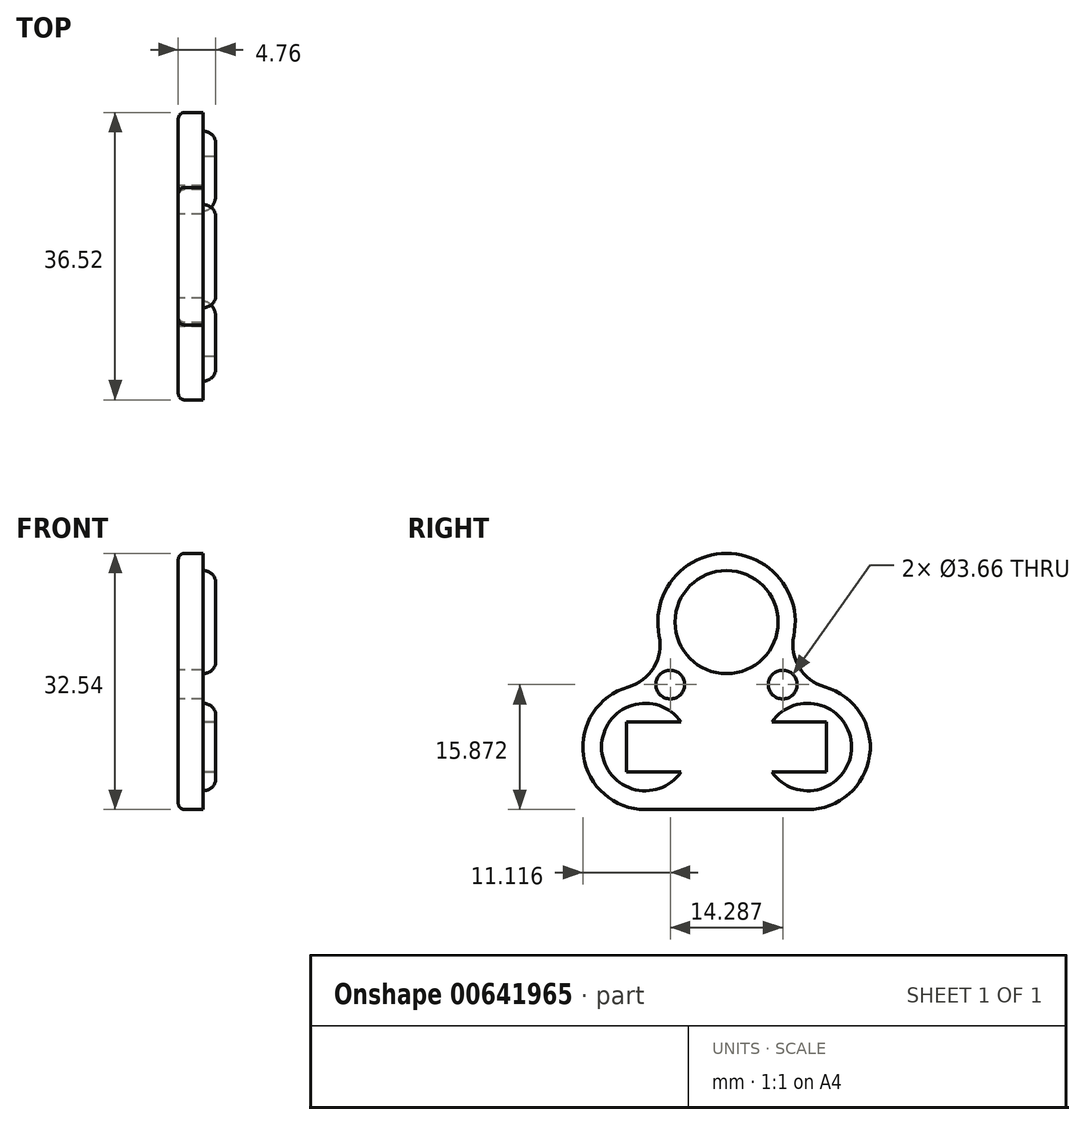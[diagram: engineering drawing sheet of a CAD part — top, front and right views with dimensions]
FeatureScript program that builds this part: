
annotation { "Feature Type Name" : "Feature", "Feature Type Description" : "" }
export const myFeature = defineFeature(function(context is Context, id is Id, definition is map)
    precondition{}
    {
        {
            var Q0;
            Q0=qCreatedBy(makeId("Right.planeOp"),FACE);
            var sketch = newSketch(context, id + "F0", { "sketchPlane" : qUnion([Q0])});
            skCircle(sketch, "E0", {"center": v(0, 0) * mm, "radius": 6.55 * mm});
            skCircle(sketch, "E1", {"center": v(0, 0) * mm, "radius": 8.73 * mm});
            skCircle(sketch, "E2", {"center": v(-10.32, -15.87) * mm, "radius": 5.56 * mm});
            skCircle(sketch, "E3", {"center": v(-10.32, -15.87) * mm, "radius": 7.94 * mm});
            skCircle(sketch, "E4", {"center": v(10.32, -15.87) * mm, "radius": 5.56 * mm});
            skCircle(sketch, "E5", {"center": v(10.32, -15.87) * mm, "radius": 7.94 * mm});
            skArc(sketch, "E6", {"start": v(-12.48, -8.24) * mm, "mid": v(-9.24, -5.77) * mm, "end": v(-8.55, -1.77) * mm});
            skArc(sketch, "E7", {"start": v(8.55, -1.77) * mm, "mid": v(9.24, -5.77) * mm, "end": v(12.48, -8.24) * mm});
            skLineSegment(sketch, "E8", {"start": v(-10.32, -23.81) * mm, "end": v(10.32, -23.81) * mm});
            skSolve(sketch);
        }
        {
            var Q0;
            Q0=makeQuery(id+"F0.imprint","IMPRINT",FACE,{"disambiguationData":[TD([[makeQuery(id+"F0.imprint","IMPRINT",EDGE,{"derivedFrom":sQuery(id+"F0.wireOp",EDGE,"E0")}),-1.0]])]});
            var Q1;
            {var subQ0=sQuery(id+"F0.wireOp",EDGE,"E6");Q1=makeQuery(id+"F0.imprint","IMPRINT",FACE,{"disambiguationData":[TD([[makeQuery(id+"F0.imprint","IMPRINT",EDGE,{"derivedFrom":subQ0}),-1.0]])]});}
            var Q2;
            Q2=makeQuery(id+"F0.imprint","IMPRINT",FACE,{"disambiguationData":[TD([[makeQuery(id+"F0.imprint","IMPRINT",EDGE,{"derivedFrom":sQuery(id+"F0.wireOp",EDGE,"E4")}),-1.0]])]});
            var Q3;
            Q3=makeQuery(id+"F0.imprint","IMPRINT",FACE,{"disambiguationData":[TD([[makeQuery(id+"F0.imprint","IMPRINT",EDGE,{"derivedFrom":sQuery(id+"F0.wireOp",EDGE,"E2")}),-1.0]])]});
            var Q4;
            Q4=makeQuery(id+"F0.imprint","IMPRINT",FACE,{"disambiguationData":[TD([[makeQuery(id+"F0.imprint","IMPRINT",EDGE,{"derivedFrom":sQuery(id+"F0.wireOp",EDGE,"E4")}),1.0]])]});
            var Q5;
            Q5=makeQuery(id+"F0.imprint","IMPRINT",FACE,{"disambiguationData":[TD([[makeQuery(id+"F0.imprint","IMPRINT",EDGE,{"derivedFrom":sQuery(id+"F0.wireOp",EDGE,"E0")}),1.0]])]});
            var Q6;
            Q6=makeQuery(id+"F0.imprint","IMPRINT",FACE,{"disambiguationData":[TD([[makeQuery(id+"F0.imprint","IMPRINT",EDGE,{"derivedFrom":sQuery(id+"F0.wireOp",EDGE,"E2")}),1.0]])]});
            extrude(context, id + "F1", {"entities" : qUnion([Q0, Q1, Q2, Q3, Q4, Q5, Q6]), "depth" : 3.17 * mm, "offsetDistance" : 25.4 * mm});
        }
        {
            var Q0;
            Q0=makeQuery(id+"F0.imprint","IMPRINT",FACE,{"disambiguationData":[TD([[makeQuery(id+"F0.imprint","IMPRINT",EDGE,{"derivedFrom":sQuery(id+"F0.wireOp",EDGE,"E4")}),1.0]])]});
            var Q1;
            Q1=makeQuery(id+"F0.imprint","IMPRINT",FACE,{"disambiguationData":[TD([[makeQuery(id+"F0.imprint","IMPRINT",EDGE,{"derivedFrom":sQuery(id+"F0.wireOp",EDGE,"E2")}),1.0]])]});
            var Q2;
            Q2=makeQuery(id+"F0.imprint","IMPRINT",FACE,{"disambiguationData":[TD([[makeQuery(id+"F0.imprint","IMPRINT",EDGE,{"derivedFrom":sQuery(id+"F0.wireOp",EDGE,"E0")}),1.0]])]});
            extrude(context, id + "F2", {"entities" : qUnion([Q0, Q1, Q2]), "operationType" : NewBodyOperationType.ADD, "depth" : 4.76 * mm, "offsetDistance" : 25.4 * mm});
        }
        {
            var Q0;
            Q0=makeQuery(id+"F2.opExtrude","CAP_EDGE",EDGE,{"disambiguationData":[OSD([sQuery(id+"F0.wireOp",EDGE,"E0")])],"isStart":false});
            var Q1;
            Q1=makeQuery(id+"F2.opExtrude","CAP_EDGE",EDGE,{"disambiguationData":[OSD([sQuery(id+"F0.wireOp",EDGE,"E4")])],"isStart":false});
            var Q2;
            Q2=makeQuery(id+"F2.opExtrude","CAP_EDGE",EDGE,{"disambiguationData":[OSD([sQuery(id+"F0.wireOp",EDGE,"E2")])],"isStart":false});
            fillet(context, id + "F3", {"entities" : qUnion([Q0, Q1, Q2]), "radius" : 1.59 * mm, "tangentPropagation" : true, "allowEdgeOverflow" : false});
        }
        {
            var Q0;
            {var subQ0=sQuery(id+"F0.wireOp",EDGE,"E6");Q0=makeQuery(id+"F0.imprint","IMPRINT",FACE,{"disambiguationData":[TD([[makeQuery(id+"F0.imprint","IMPRINT",EDGE,{"derivedFrom":subQ0}),-1.0]])]});}
            var sketch = newSketch(context, id + "F4", { "sketchPlane" : qUnion([Q0])});
            skPoint(sketch, "E9", {"position": v(-7.14, -7.94) * mm});
            skPoint(sketch, "E10", {"position": v(7.14, -7.94) * mm});
            skSolve(sketch);
        }
        {
            var Q0;
            Q0=sQuery(id+"F4.wireOp",VERTEX,"E10");
            var Q1;
            Q1=sQuery(id+"F4.wireOp",VERTEX,"E9");
            var Q2;
            Q2=makeQuery(id+"F1.opExtrude","SWEPT_BODY",BODY,{"disambiguationData":[OSD([sQuery(id+"F0.wireOp",EDGE,"E1"),sQuery(id+"F0.wireOp",EDGE,"E3"),sQuery(id+"F0.wireOp",EDGE,"E5"),sQuery(id+"F0.wireOp",EDGE,"E6"),sQuery(id+"F0.wireOp",EDGE,"E7"),sQuery(id+"F0.wireOp",EDGE,"E8")])]});
            hole(context, id + "F5", {"style" : HoleStyle.SIMPLE, "endStyle" : HoleEndStyle.THROUGH, "oppositeDirection" : true, "holeDiameter" : 3.66 * mm, "majorDiameter" : 6.35 * mm, "isTappedThrough" : true, "tappedDepth" : 12.7 * mm, "tapClearance" : 3, "locations" : qUnion([Q0, Q1]), "scope" : qUnion([Q2])});
        }
        {
            var Q0;
            Q0=makeQuery(id+"F2.opExtrude","CAP_FACE",FACE,{"disambiguationData":[OSD([sQuery(id+"F0.wireOp",EDGE,"E4")])],"isStart":false});
            var sketch = newSketch(context, id + "F6", { "sketchPlane" : qUnion([Q0])});
            skLineSegment(sketch, "E11.bottom", {"start": v(-12.7, -12.7) * mm, "end": v(12.7, -12.7) * mm});
            skLineSegment(sketch, "E11.top", {"start": v(-12.7, -19.05) * mm, "end": v(12.7, -19.05) * mm});
            skLineSegment(sketch, "E11.left", {"start": v(-12.7, -12.7) * mm, "end": v(-12.7, -19.05) * mm});
            skLineSegment(sketch, "E11.right", {"start": v(12.7, -12.7) * mm, "end": v(12.7, -19.05) * mm});
            skSolve(sketch);
        }
        {
            var Q0;
            {var subQ0=sQuery(id+"F6.wireOp",EDGE,"E11.right");Q0=makeQuery(id+"F6.imprint","IMPRINT",FACE,{"disambiguationData":[TD([[makeQuery(id+"F6.imprint","IMPRINT",EDGE,{"derivedFrom":subQ0}),-1.0]])]});}
            var Q1;
            {var subQ0=sQuery(id+"F6.wireOp",EDGE,"E11.left");Q1=makeQuery(id+"F6.imprint","IMPRINT",FACE,{"disambiguationData":[TD([[makeQuery(id+"F6.imprint","IMPRINT",EDGE,{"derivedFrom":subQ0}),1.0]])]});}
            extrude(context, id + "F7", {"entities" : qUnion([Q0, Q1]), "operationType" : NewBodyOperationType.REMOVE, "oppositeDirection" : true, "depth" : 1.59 * mm, "offsetDistance" : 25.4 * mm});
        }
        {
            var Q0;
            Q0=makeQuery(id+"F1.opExtrude","CAP_EDGE",EDGE,{"disambiguationData":[OSD([sQuery(id+"F0.wireOp",EDGE,"E1")])],"isStart":true});
            fillet(context, id + "F8", {"entities" : qUnion([Q0]), "radius" : 0.8 * mm, "tangentPropagation" : true, "allowEdgeOverflow" : false});
        }
    });
